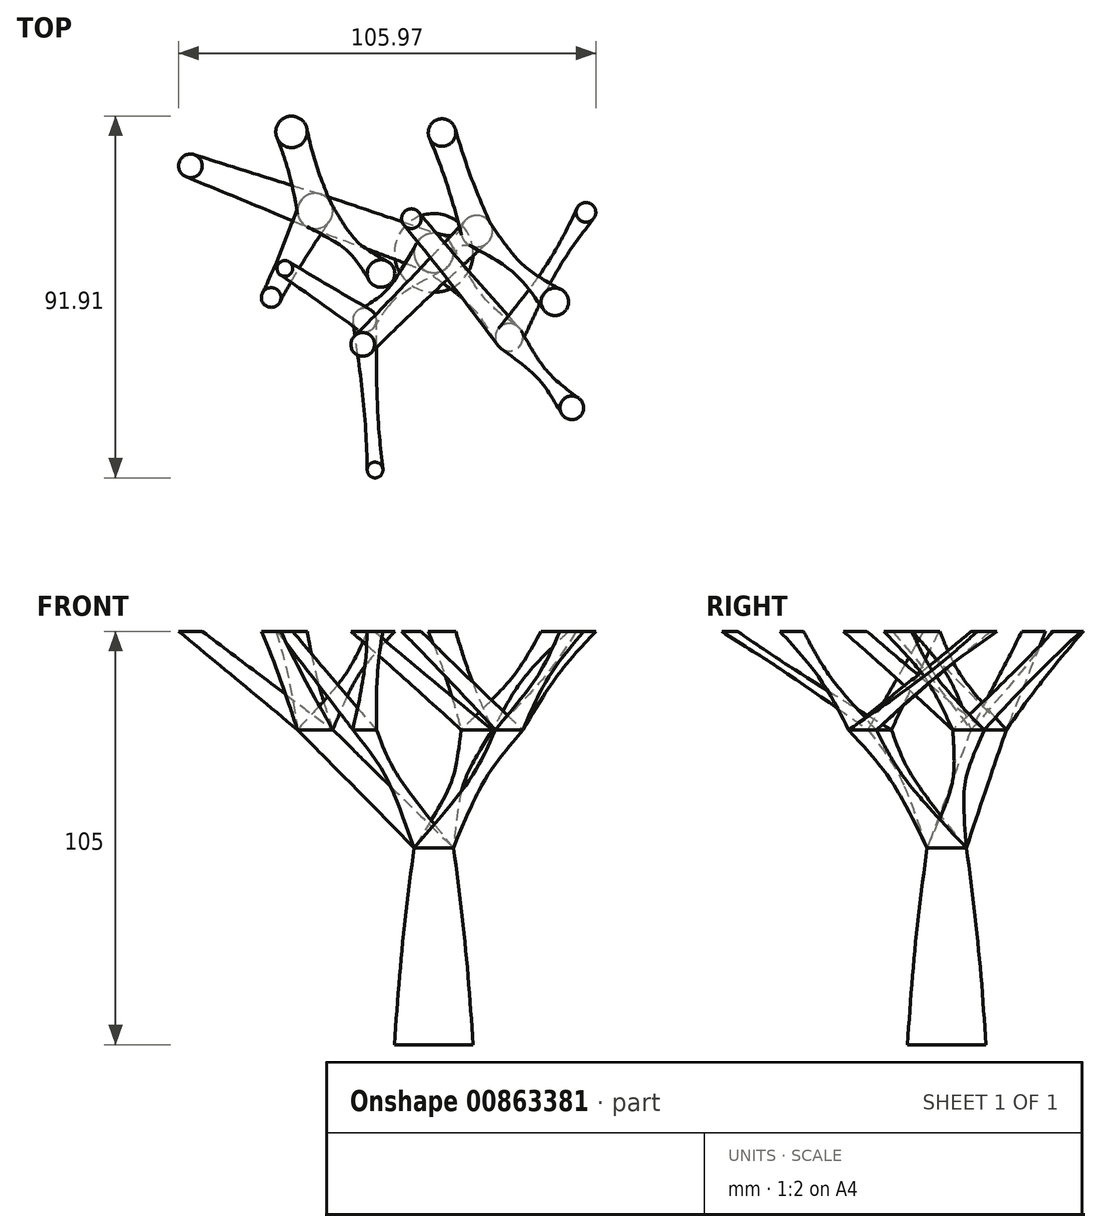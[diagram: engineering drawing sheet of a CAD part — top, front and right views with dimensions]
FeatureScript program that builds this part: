
annotation { "Feature Type Name" : "Feature", "Feature Type Description" : "" }
export const myFeature = defineFeature(function(context is Context, id is Id, definition is map)
    precondition{}
    {
        {
            var Q0;
            Q0=qCreatedBy(makeId("Top.planeOp"),FACE);
            var sketch = newSketch(context, id + "F0", { "sketchPlane" : qUnion([Q0])});
            skCircle(sketch, "E0", {"center": v(0, 0) * mm, "radius": 35 * mm});
            skCircle(sketch, "E1", {"center": v(0, 0) * mm, "radius": 10 * mm});
            skSolve(sketch);
        }
        {
            var Q0;
            Q0=qCreatedBy(makeId("Top.planeOp"),FACE);
            cPlane(context, id + "F1", {"entities" : qUnion([Q0]), "cplaneType" : CPlaneType.OFFSET, "offset" : 30 * mm, "width" : 150 * mm, "height" : 150 * mm});
        }
        {
            var Q0;
            Q0=qCreatedBy(id+"F1.planeOp",FACE);
            var sketch = newSketch(context, id + "F2", { "sketchPlane" : qUnion([Q0])});
            skCircle(sketch, "E2", {"center": v(0, 0) * mm, "radius": 7.5 * mm});
            skSolve(sketch);
        }
        {
            var Q0;
            Q0=qCreatedBy(id+"F1.planeOp",FACE);
            cPlane(context, id + "F3", {"entities" : qUnion([Q0]), "cplaneType" : CPlaneType.OFFSET, "offset" : 20 * mm, "width" : 150 * mm, "height" : 150 * mm});
        }
        {
            var Q0;
            Q0=qCreatedBy(id+"F3.planeOp",FACE);
            var sketch = newSketch(context, id + "F4", { "sketchPlane" : qUnion([Q0])});
            skCircle(sketch, "E3", {"center": v(0, 0) * mm, "radius": 5 * mm});
            skSolve(sketch);
        }
        {
            var Q0;
            Q0=qCreatedBy(id+"F3.planeOp",FACE);
            cPlane(context, id + "F5", {"entities" : qUnion([Q0]), "cplaneType" : CPlaneType.OFFSET, "offset" : 30 * mm, "width" : 150 * mm, "height" : 150 * mm});
        }
        {
            var Q0;
            Q0=qCreatedBy(id+"F5.planeOp",FACE);
            var sketch = newSketch(context, id + "F6", { "sketchPlane" : qUnion([Q0])});
            skCircle(sketch, "E4", {"center": v(-30.15, 10.65) * mm, "radius": 4.5 * mm});
            skCircle(sketch, "E5", {"center": v(19.12, -21.43) * mm, "radius": 3.5 * mm});
            skCircle(sketch, "E6", {"center": v(10.9, 5.52) * mm, "radius": 4 * mm});
            skCircle(sketch, "E7", {"center": v(-17.58, -17.06) * mm, "radius": 3 * mm});
            skSolve(sketch);
        }
        {
            var Q0;
            Q0=makeQuery(id+"F0.imprint","IMPRINT",FACE,{"disambiguationData":[TD([[makeQuery(id+"F0.imprint","IMPRINT",EDGE,{"derivedFrom":sQuery(id+"F0.wireOp",EDGE,"E1")}),1.0]])]});
            var Q1;
            Q1=makeQuery(id+"F2.imprint","IMPRINT",FACE,{"disambiguationData":[TD([[makeQuery(id+"F2.imprint","IMPRINT",EDGE,{"derivedFrom":sQuery(id+"F2.wireOp",EDGE,"E2")}),1.0]])]});
            var Q2;
            Q2=makeQuery(id+"F4.imprint","IMPRINT",FACE,{"disambiguationData":[TD([[makeQuery(id+"F4.imprint","IMPRINT",EDGE,{"derivedFrom":sQuery(id+"F4.wireOp",EDGE,"E3")}),1.0]])]});
            loft(context, id + "F7", {"sheetProfilesArray" : [{ "sheetProfileEntities" : qUnion([Q0]) }, { "sheetProfileEntities" : qUnion([Q1]) }, { "sheetProfileEntities" : qUnion([Q2]) }]});
        }
        {
            var Q1;
            Q1=makeQuery(id+"F7.opLoft","CAP_FACE",FACE,{"disambiguationData":[OSD([makeQuery(id+"F4.imprint","IMPRINT",FACE,{"disambiguationData":[TD([[makeQuery(id+"F4.imprint","IMPRINT",EDGE,{"derivedFrom":sQuery(id+"F4.wireOp",EDGE,"E3")}),1.0]])]})])],"isStart":true});
            var Q2;
            Q2=makeQuery(id+"F6.imprint","IMPRINT",FACE,{"disambiguationData":[TD([[makeQuery(id+"F6.imprint","IMPRINT",EDGE,{"derivedFrom":sQuery(id+"F6.wireOp",EDGE,"E4")}),1.0]])]});
            loft(context, id + "F8", {"sheetProfilesArray" : [{ "sheetProfileEntities" : qUnion([Q1]) }, { "sheetProfileEntities" : qUnion([Q2]) }]});
        }
        {
            var Q1;
            Q1=makeQuery(id+"F7.opLoft","CAP_FACE",FACE,{"disambiguationData":[OSD([makeQuery(id+"F4.imprint","IMPRINT",FACE,{"disambiguationData":[TD([[makeQuery(id+"F4.imprint","IMPRINT",EDGE,{"derivedFrom":sQuery(id+"F4.wireOp",EDGE,"E3")}),1.0]])]})])],"isStart":true});
            var Q2;
            Q2=makeQuery(id+"F6.imprint","IMPRINT",FACE,{"disambiguationData":[TD([[makeQuery(id+"F6.imprint","IMPRINT",EDGE,{"derivedFrom":sQuery(id+"F6.wireOp",EDGE,"E6")}),1.0]])]});
            loft(context, id + "F9", {"sheetProfilesArray" : [{ "sheetProfileEntities" : qUnion([Q1]) }, { "sheetProfileEntities" : qUnion([Q2]) }]});
        }
        {
            var Q1;
            Q1=makeQuery(id+"F7.opLoft","CAP_FACE",FACE,{"disambiguationData":[OSD([makeQuery(id+"F4.imprint","IMPRINT",FACE,{"disambiguationData":[TD([[makeQuery(id+"F4.imprint","IMPRINT",EDGE,{"derivedFrom":sQuery(id+"F4.wireOp",EDGE,"E3")}),1.0]])]})])],"isStart":true});
            var Q2;
            Q2=makeQuery(id+"F6.imprint","IMPRINT",FACE,{"disambiguationData":[TD([[makeQuery(id+"F6.imprint","IMPRINT",EDGE,{"derivedFrom":sQuery(id+"F6.wireOp",EDGE,"E5")}),1.0]])]});
            loft(context, id + "F10", {"sheetProfilesArray" : [{ "sheetProfileEntities" : qUnion([Q1]) }, { "sheetProfileEntities" : qUnion([Q2]) }]});
        }
        {
            var Q1;
            Q1=makeQuery(id+"F6.imprint","IMPRINT",FACE,{"disambiguationData":[TD([[makeQuery(id+"F6.imprint","IMPRINT",EDGE,{"derivedFrom":sQuery(id+"F6.wireOp",EDGE,"E7")}),1.0]])]});
            var Q2;
            Q2=makeQuery(id+"F7.opLoft","CAP_FACE",FACE,{"disambiguationData":[OSD([makeQuery(id+"F4.imprint","IMPRINT",FACE,{"disambiguationData":[TD([[makeQuery(id+"F4.imprint","IMPRINT",EDGE,{"derivedFrom":sQuery(id+"F4.wireOp",EDGE,"E3")}),1.0]])]})])],"isStart":true});
            loft(context, id + "F11", {"sheetProfilesArray" : [{ "sheetProfileEntities" : qUnion([Q1]) }, { "sheetProfileEntities" : qUnion([Q2]) }]});
        }
        {
            var Q0;
            Q0=qCreatedBy(id+"F5.planeOp",FACE);
            cPlane(context, id + "F12", {"entities" : qUnion([Q0]), "cplaneType" : CPlaneType.OFFSET, "offset" : 25 * mm, "width" : 150 * mm, "height" : 150 * mm});
        }
        {
            var Q0;
            Q0=qCreatedBy(id+"F12.planeOp",FACE);
            var sketch = newSketch(context, id + "F13", { "sketchPlane" : qUnion([Q0])});
            skCircle(sketch, "E8", {"center": v(-41.32, -11.33) * mm, "radius": 2.5 * mm});
            skCircle(sketch, "E9", {"center": v(-61.82, 22.12) * mm, "radius": 3 * mm});
            skCircle(sketch, "E10", {"center": v(-36.14, 30.75) * mm, "radius": 4 * mm});
            skCircle(sketch, "E11", {"center": v(-37.84, -3.94) * mm, "radius": 2 * mm});
            skCircle(sketch, "E12", {"center": v(-14.92, -55.16) * mm, "radius": 2 * mm});
            skCircle(sketch, "E13", {"center": v(35.06, -39.35) * mm, "radius": 3 * mm});
            skCircle(sketch, "E14", {"center": v(38.65, 10.3) * mm, "radius": 2.5 * mm});
            skCircle(sketch, "E15", {"center": v(2.08, 30.58) * mm, "radius": 3.5 * mm});
            skCircle(sketch, "E16", {"center": v(30.75, -12.43) * mm, "radius": 3.5 * mm});
            skCircle(sketch, "E17", {"center": v(-5.7, 8.7) * mm, "radius": 2.5 * mm});
            skCircle(sketch, "E18", {"center": v(-18.07, -23.25) * mm, "radius": 3 * mm});
            skCircle(sketch, "E19", {"center": v(-13.41, -5.24) * mm, "radius": 3.5 * mm});
            skSolve(sketch);
        }
        {
            var Q0;
            Q0=makeQuery(id+"F6.imprint","IMPRINT",FACE,{"disambiguationData":[TD([[makeQuery(id+"F6.imprint","IMPRINT",EDGE,{"derivedFrom":sQuery(id+"F6.wireOp",EDGE,"E4")}),1.0]])]});
            var Q1;
            Q1=makeQuery(id+"F13.imprint","IMPRINT",FACE,{"disambiguationData":[TD([[makeQuery(id+"F13.imprint","IMPRINT",EDGE,{"derivedFrom":sQuery(id+"F13.wireOp",EDGE,"E10")}),1.0]])]});
            loft(context, id + "F14", {"sheetProfilesArray" : [{ "sheetProfileEntities" : qUnion([Q0]) }, { "sheetProfileEntities" : qUnion([Q1]) }]});
        }
        {
            var Q0;
            Q0=makeQuery(id+"F6.imprint","IMPRINT",FACE,{"disambiguationData":[TD([[makeQuery(id+"F6.imprint","IMPRINT",EDGE,{"derivedFrom":sQuery(id+"F6.wireOp",EDGE,"E4")}),1.0]])]});
            var Q1;
            Q1=makeQuery(id+"F13.imprint","IMPRINT",FACE,{"disambiguationData":[TD([[makeQuery(id+"F13.imprint","IMPRINT",EDGE,{"derivedFrom":sQuery(id+"F13.wireOp",EDGE,"E9")}),1.0]])]});
            loft(context, id + "F15", {"sheetProfilesArray" : [{ "sheetProfileEntities" : qUnion([Q0]) }, { "sheetProfileEntities" : qUnion([Q1]) }]});
        }
        {
            var Q1;
            Q1=makeQuery(id+"F6.imprint","IMPRINT",FACE,{"disambiguationData":[TD([[makeQuery(id+"F6.imprint","IMPRINT",EDGE,{"derivedFrom":sQuery(id+"F6.wireOp",EDGE,"E4")}),1.0]])]});
            var Q2;
            Q2=makeQuery(id+"F13.imprint","IMPRINT",FACE,{"disambiguationData":[TD([[makeQuery(id+"F13.imprint","IMPRINT",EDGE,{"derivedFrom":sQuery(id+"F13.wireOp",EDGE,"E8")}),1.0]])]});
            loft(context, id + "F16", {"sheetProfilesArray" : [{ "sheetProfileEntities" : qUnion([Q1]) }, { "sheetProfileEntities" : qUnion([Q2]) }]});
        }
        {
            var Q0;
            Q0=makeQuery(id+"F6.imprint","IMPRINT",FACE,{"disambiguationData":[TD([[makeQuery(id+"F6.imprint","IMPRINT",EDGE,{"derivedFrom":sQuery(id+"F6.wireOp",EDGE,"E7")}),1.0]])]});
            var Q1;
            Q1=makeQuery(id+"F13.imprint","IMPRINT",FACE,{"disambiguationData":[TD([[makeQuery(id+"F13.imprint","IMPRINT",EDGE,{"derivedFrom":sQuery(id+"F13.wireOp",EDGE,"E11")}),1.0]])]});
            loft(context, id + "F17", {"sheetProfilesArray" : [{ "sheetProfileEntities" : qUnion([Q0]) }, { "sheetProfileEntities" : qUnion([Q1]) }]});
        }
        {
            var Q0;
            Q0=makeQuery(id+"F6.imprint","IMPRINT",FACE,{"disambiguationData":[TD([[makeQuery(id+"F6.imprint","IMPRINT",EDGE,{"derivedFrom":sQuery(id+"F6.wireOp",EDGE,"E7")}),1.0]])]});
            var Q1;
            Q1=makeQuery(id+"F13.imprint","IMPRINT",FACE,{"disambiguationData":[TD([[makeQuery(id+"F13.imprint","IMPRINT",EDGE,{"derivedFrom":sQuery(id+"F13.wireOp",EDGE,"E12")}),1.0]])]});
            loft(context, id + "F18", {"sheetProfilesArray" : [{ "sheetProfileEntities" : qUnion([Q0]) }, { "sheetProfileEntities" : qUnion([Q1]) }]});
        }
        {
            var Q0;
            Q0=makeQuery(id+"F6.imprint","IMPRINT",FACE,{"disambiguationData":[TD([[makeQuery(id+"F6.imprint","IMPRINT",EDGE,{"derivedFrom":sQuery(id+"F6.wireOp",EDGE,"E5")}),1.0]])]});
            var Q1;
            Q1=makeQuery(id+"F13.imprint","IMPRINT",FACE,{"disambiguationData":[TD([[makeQuery(id+"F13.imprint","IMPRINT",EDGE,{"derivedFrom":sQuery(id+"F13.wireOp",EDGE,"E17")}),1.0]])]});
            loft(context, id + "F19", {"sheetProfilesArray" : [{ "sheetProfileEntities" : qUnion([Q0]) }, { "sheetProfileEntities" : qUnion([Q1]) }]});
        }
        {
            var Q0;
            Q0=makeQuery(id+"F6.imprint","IMPRINT",FACE,{"disambiguationData":[TD([[makeQuery(id+"F6.imprint","IMPRINT",EDGE,{"derivedFrom":sQuery(id+"F6.wireOp",EDGE,"E5")}),1.0]])]});
            var Q1;
            Q1=makeQuery(id+"F13.imprint","IMPRINT",FACE,{"disambiguationData":[TD([[makeQuery(id+"F13.imprint","IMPRINT",EDGE,{"derivedFrom":sQuery(id+"F13.wireOp",EDGE,"E13")}),1.0]])]});
            loft(context, id + "F20", {"sheetProfilesArray" : [{ "sheetProfileEntities" : qUnion([Q0]) }, { "sheetProfileEntities" : qUnion([Q1]) }]});
        }
        {
            var Q0;
            Q0=makeQuery(id+"F6.imprint","IMPRINT",FACE,{"disambiguationData":[TD([[makeQuery(id+"F6.imprint","IMPRINT",EDGE,{"derivedFrom":sQuery(id+"F6.wireOp",EDGE,"E5")}),1.0]])]});
            var Q1;
            Q1=makeQuery(id+"F13.imprint","IMPRINT",FACE,{"disambiguationData":[TD([[makeQuery(id+"F13.imprint","IMPRINT",EDGE,{"derivedFrom":sQuery(id+"F13.wireOp",EDGE,"E14")}),1.0]])]});
            loft(context, id + "F21", {"sheetProfilesArray" : [{ "sheetProfileEntities" : qUnion([Q0]) }, { "sheetProfileEntities" : qUnion([Q1]) }]});
        }
        {
            var Q0;
            Q0=makeQuery(id+"F6.imprint","IMPRINT",FACE,{"disambiguationData":[TD([[makeQuery(id+"F6.imprint","IMPRINT",EDGE,{"derivedFrom":sQuery(id+"F6.wireOp",EDGE,"E6")}),1.0]])]});
            var Q1;
            Q1=makeQuery(id+"F13.imprint","IMPRINT",FACE,{"disambiguationData":[TD([[makeQuery(id+"F13.imprint","IMPRINT",EDGE,{"derivedFrom":sQuery(id+"F13.wireOp",EDGE,"E15")}),1.0]])]});
            loft(context, id + "F22", {"sheetProfilesArray" : [{ "sheetProfileEntities" : qUnion([Q0]) }, { "sheetProfileEntities" : qUnion([Q1]) }]});
        }
        {
            var Q1;
            Q1=makeQuery(id+"F6.imprint","IMPRINT",FACE,{"disambiguationData":[TD([[makeQuery(id+"F6.imprint","IMPRINT",EDGE,{"derivedFrom":sQuery(id+"F6.wireOp",EDGE,"E6")}),1.0]])]});
            var Q2;
            Q2=makeQuery(id+"F13.imprint","IMPRINT",FACE,{"disambiguationData":[TD([[makeQuery(id+"F13.imprint","IMPRINT",EDGE,{"derivedFrom":sQuery(id+"F13.wireOp",EDGE,"E18")}),1.0]])]});
            loft(context, id + "F23", {"sheetProfilesArray" : [{ "sheetProfileEntities" : qUnion([Q1]) }, { "sheetProfileEntities" : qUnion([Q2]) }]});
        }
        {
            var Q0;
            Q0=makeQuery(id+"F6.imprint","IMPRINT",FACE,{"disambiguationData":[TD([[makeQuery(id+"F6.imprint","IMPRINT",EDGE,{"derivedFrom":sQuery(id+"F6.wireOp",EDGE,"E6")}),1.0]])]});
            var Q1;
            Q1=makeQuery(id+"F13.imprint","IMPRINT",FACE,{"disambiguationData":[TD([[makeQuery(id+"F13.imprint","IMPRINT",EDGE,{"derivedFrom":sQuery(id+"F13.wireOp",EDGE,"E16")}),1.0]])]});
            loft(context, id + "F24", {"sheetProfilesArray" : [{ "sheetProfileEntities" : qUnion([Q0]) }, { "sheetProfileEntities" : qUnion([Q1]) }]});
        }
        {
            var Q0;
            Q0=makeQuery(id+"F6.imprint","IMPRINT",FACE,{"disambiguationData":[TD([[makeQuery(id+"F6.imprint","IMPRINT",EDGE,{"derivedFrom":sQuery(id+"F6.wireOp",EDGE,"E4")}),1.0]])]});
            var Q1;
            Q1=makeQuery(id+"F13.imprint","IMPRINT",FACE,{"disambiguationData":[TD([[makeQuery(id+"F13.imprint","IMPRINT",EDGE,{"derivedFrom":sQuery(id+"F13.wireOp",EDGE,"E19")}),1.0]])]});
            loft(context, id + "F25", {"sheetProfilesArray" : [{ "sheetProfileEntities" : qUnion([Q0]) }, { "sheetProfileEntities" : qUnion([Q1]) }]});
        }
    });
